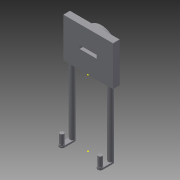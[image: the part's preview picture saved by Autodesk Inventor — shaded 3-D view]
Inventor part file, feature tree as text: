
AUTODESK INVENTOR PART (.ipt)
format: ipt  version: 2015 SP2 (Build 190223200, 223)  size: 163,840 bytes
history: native  units: mm
features: sketch x11, extrude x9
ambient origin geometry x8: Origin, YZ Plane, XZ Plane, XY Plane, X Axis, Y Axis, Z Axis, Center Point
bodies: Solid1 (feature_tree)
feature tree (20):
  sketch  "Sketch1"  dims[d0=5.1mm d1=1.0mm]
  sketch  "Sketch2"  dims[d2=15.0mm d3=12.0mm]
  extrude  "Extrusion1"  Depth=1.0mm
  extrude  "Extrusion2"  Depth=12.0mm
  extrude  "Extrusion4"  Depth=2.0mm TaperAngle=0.0deg
  extrude  "Extrusion5"  Depth=4.0mm TaperAngle=0.0deg
  extrude  "Extrusion6"  Depth=5.1mm
  extrude  "Extrusion7"  Depth=3.0mm TaperAngle=0.0deg
  extrude  "Extrusion8"  Depth=20.0mm TaperAngle=0.0deg
  sketch  "Sketch15"  dims[d25=1.5mm d26=1.5mm]
  extrude  "Extrusion9"  Depth=1.5mm
  extrude  "Extrusion10"  Depth=0.5mm
  sketch  "Sketch20"  dims[d32=1.35mm d33=1.35mm d34=1.35mm d35=1.35mm d36=0.25mm d37=0.0mm]
  sketch  "Sketch3"  dims[d4=10.0mm d5=2.0mm d6=0.0mm]
  sketch  "Sketch7"  dims[d7=2.0mm d8=0.0mm d11=4.0mm d12=0.0mm]
  sketch  "Sketch8"  dims[d13=3.0mm d14=0.0mm d15=5.1mm]
  sketch  "Sketch9"  dims[d16=1.0mm d17=3.0mm d18=0.0mm]
  sketch  "Sketch14"  dims[d19=1.5mm d20=20.0mm d21=0.0mm]
  sketch  "Sketch17"  dims[d27=0.5mm d28=0.0mm d29=1.2mm]
  sketch  "Sketch19"  dims[d30=3.0mm d31=0.0mm]
